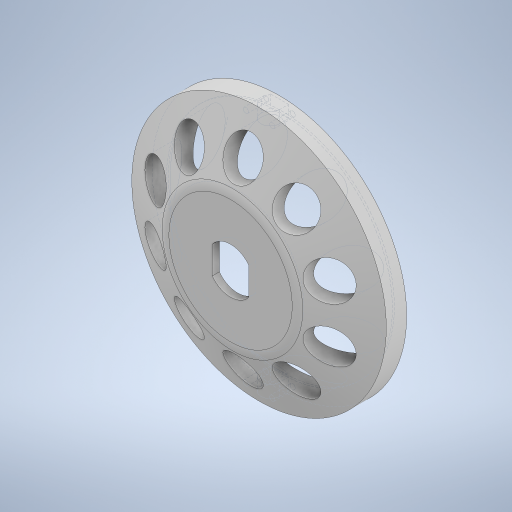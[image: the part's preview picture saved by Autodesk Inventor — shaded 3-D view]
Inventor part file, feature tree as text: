
AUTODESK INVENTOR PART (.ipt)
format: ipt  version: 2023 (Build 270158000, 158)  size: 429,056 bytes
history: native  units: mm
features: sketch x6, extrude x5, revolve x1, fillet x1, plane x1, pattern_circular x1, mirror x1
ambient origin geometry x8: Origin, YZ Plane, XZ Plane, XY Plane, X Axis, Y Axis, Z Axis, Center Point
bodies: Solid1 (feature_tree)
feature tree (16):
  extrude  "Extrusion1"  Depth=18.0mm
  revolve  "Revolution1"  [1 undecoded]
  fillet  "Fillet1"  Radius=7.0mm
  plane  "Work Plane2"
  extrude  "Extrusion2"  Depth=11.0mm
  sketch  "Sketch4"  dims[d11=30.0mm d12=90.0deg]
  extrude  "Extrusion3"  TaperAngle=90.0deg  [1 undecoded]
  pattern_circular  "Circular Pattern1"  [2 undecoded]
  mirror  "Mirror1"
  extrude  "Extrusion4"  Depth=10.0mm
  extrude  "Extrusion5"  TaperAngle=0.0deg  [1 undecoded]
  sketch  "Sketch1"  dims[d0=22.5mm d1=18.0mm]
  sketch  "Sketch2"  dims[d2=65.0mm d3=3.5mm d4=0.0mm d8=7.0mm]
  sketch  "Sketch3"  dims[d9=25.0mm d10=11.0mm]
  sketch  "Sketch5"  dims[d13=10.0mm]
  sketch  "Sketch6"  dims[d14=9.0mm d19=61.0mm d20=6.0mm d21=0.0mm d22=1.0mm d23=0.0mm d24=0.0mm d25=45.0mm d26=18.0mm d27=100.0mm d28=360.0deg d30=1.0mm d31=0.0mm d32=2.0mm d33=2.5mm d34=10.0mm d35=0.0mm]
note: 5 required parameter values undecoded (feature->parameter linkage not recoverable at this tier; creation-order binding heuristic only, values carry confidence <= 0.55)